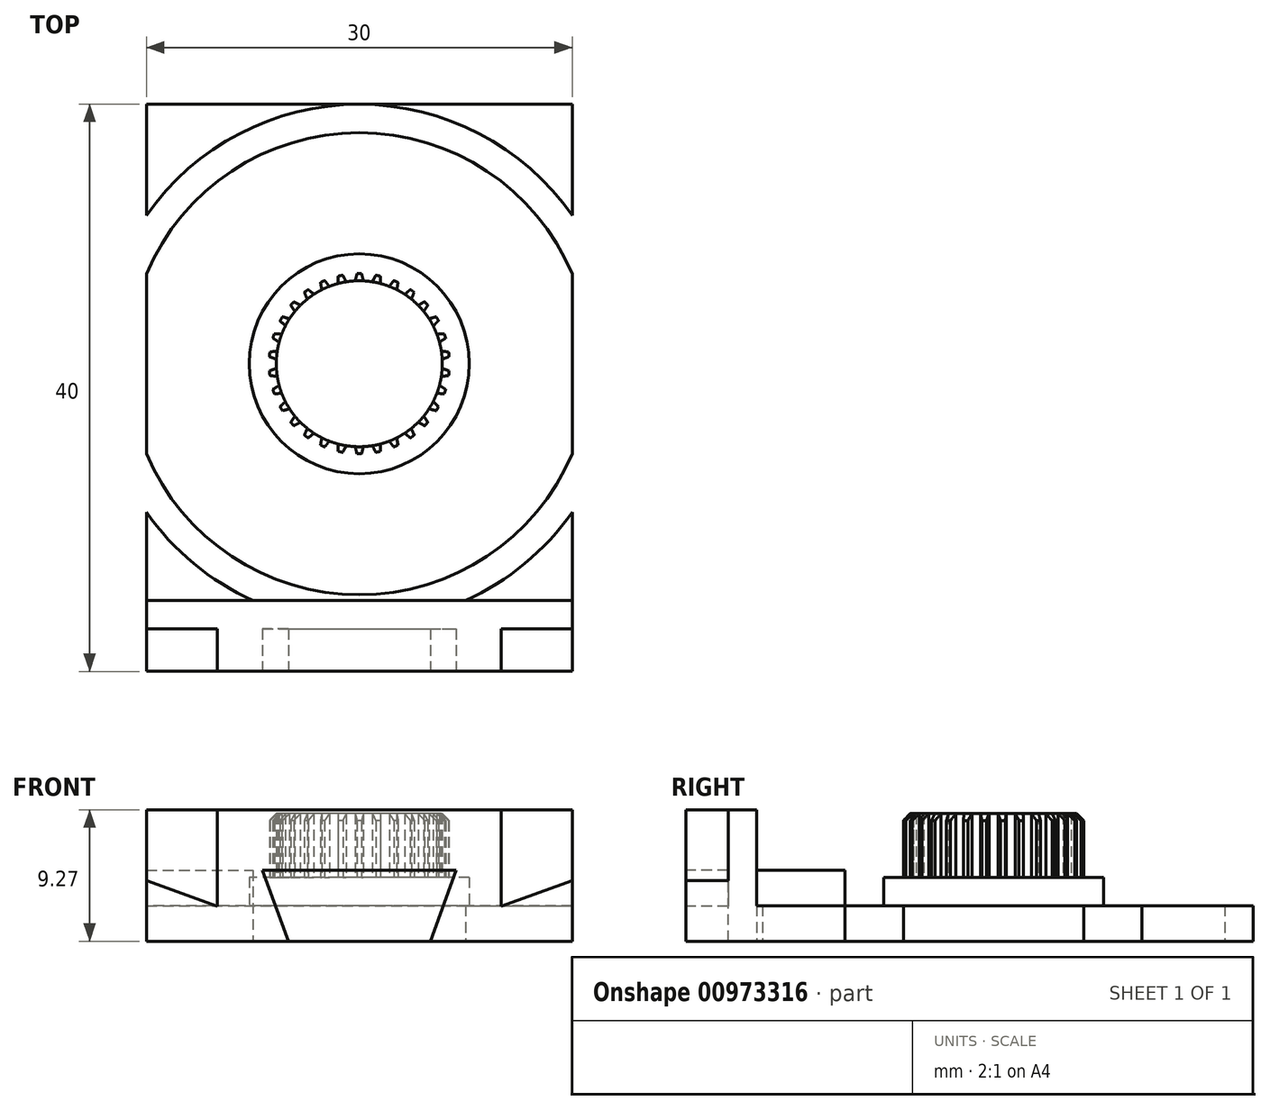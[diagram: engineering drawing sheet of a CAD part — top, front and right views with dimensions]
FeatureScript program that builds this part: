
annotation { "Feature Type Name" : "Feature", "Feature Type Description" : "" }
export const myFeature = defineFeature(function(context is Context, id is Id, definition is map)
    precondition{}
    {
        {
            var Q0;
            Q0=qCreatedBy(makeId("Top.planeOp"),FACE);
            var sketch = newSketch(context, id + "F0", { "sketchPlane" : qUnion([Q0])});
            skLineSegment(sketch, "E0.bottom", {"start": v(-15, 18.31) * mm, "end": v(15, 18.31) * mm});
            skLineSegment(sketch, "E0.top", {"start": v(-15, -21.69) * mm, "end": v(15, -21.69) * mm});
            skLineSegment(sketch, "E0.left", {"start": v(-15, 18.31) * mm, "end": v(-15, -21.69) * mm});
            skLineSegment(sketch, "E0.right", {"start": v(15, 18.31) * mm, "end": v(15, -21.69) * mm});
            skCircle(sketch, "E1", {"center": v(0, 0) * mm, "radius": 14.29 * mm, "construction": true});
            skLineSegment(sketch, "E2", {"start": v(-15, -16.69) * mm, "end": v(15, -16.69) * mm});
            skCircle(sketch, "E3", {"center": v(0, 0) * mm, "radius": 7.75 * mm});
            skCircle(sketch, "E4", {"center": v(0, 0) * mm, "radius": 6.35 * mm});
            skCircle(sketch, "E5", {"center": v(0, 0) * mm, "radius": 5.85 * mm});
            skLineSegment(sketch, "E6", {"start": v(6.33, 0.5) * mm, "end": v(5.84, 0.32) * mm});
            skLineSegment(sketch, "E7.MirrorCS", {"start": v(6.33, -0.5) * mm, "end": v(5.84, -0.32) * mm});
            skLineSegment(sketch, "E8", {"start": v(0, 0) * mm, "end": v(0, 18.29) * mm, "construction": true});
            skLineSegment(sketch, "E9", {"start": v(0, 0) * mm, "end": v(0, -14.29) * mm, "construction": true});
            skPoint(sketch, "E10.start.orphan", {"position": v(-15, 0) * mm});
            skCircle(sketch, "E11", {"center": v(0, 0) * mm, "radius": 16.29 * mm});
            skCircle(sketch, "E12", {"center": v(0, 0) * mm, "radius": 18.29 * mm});
            skSolve(sketch);
        }
        {
            var Q0;
            Q0=makeQuery(id+"F0.imprint","IMPRINT",FACE,{"disambiguationData":[TD([[makeQuery(id+"F0.imprint","IMPRINT",EDGE,{"derivedFrom":sQuery(id+"F0.wireOp",EDGE,"vQMhKaP6-cxV4-EDMz-RZqz-IjqFTc3130Nv")}),-1.0]])]});
            var Q1;
            Q1=makeQuery(id+"F0.imprint","IMPRINT",FACE,{"disambiguationData":[TD([[makeQuery(id+"F0.imprint","IMPRINT",EDGE,{"derivedFrom":sQuery(id+"F0.wireOp",EDGE,"E3")}),-1.0]])]});
            var Q2;
            {var subQ0=sQuery(id+"F0.wireOp",EDGE,"E2");Q2=makeQuery(id+"F0.imprint","IMPRINT",FACE,{"disambiguationData":[TD([[makeQuery(id+"F0.imprint","IMPRINT",EDGE,{"derivedFrom":subQ0}),1.0]])]});}
            var Q3;
            {var subQ1=sQuery(id+"F0.wireOp",EDGE,"E0.left");var subQ5=sQuery(id+"F0.wireOp",EDGE,"E12");var subQ10=makeQuery(id+"F0.imprint","INTERSECT",VERTEX,{"disambiguationData":[OD(1.0)],"derivedFrom":[subQ1,subQ5]});Q3=makeQuery(id+"F0.imprint","IMPRINT",FACE,{"disambiguationData":[TD([[makeQuery(id+"F0.imprint","IMPRINT",EDGE,{"disambiguationData":[TD([[subQ10,1.0]])],"derivedFrom":subQ1}),1.0]])]});}
            extrude(context, id + "F1", {"entities" : qUnion([Q0, Q1, Q2, Q3]), "depth" : 2.5 * mm, "offsetDistance" : 25 * mm});
        }
        {
            var Q0;
            Q0=makeQuery(id+"F0.imprint","IMPRINT",FACE,{"disambiguationData":[TD([[makeQuery(id+"F0.imprint","IMPRINT",EDGE,{"derivedFrom":sQuery(id+"F0.wireOp",EDGE,"E3")}),1.0]])]});
            extrude(context, id + "F2", {"entities" : qUnion([Q0]), "operationType" : NewBodyOperationType.ADD, "depth" : 4.5 * mm, "offsetDistance" : 25 * mm});
        }
        {
            var Q0;
            Q0=makeQuery(id+"F0.imprint","IMPRINT",FACE,{"disambiguationData":[TD([[makeQuery(id+"F0.imprint","IMPRINT",EDGE,{"derivedFrom":sQuery(id+"F0.wireOp",EDGE,"E4")}),1.0]])]});
            var Q1;
            {var subQ0=sQuery(id+"F0.wireOp",EDGE,"E5");var subQ1=makeQuery(id+"F0.imprint","INTERSECT",VERTEX,{"derivedFrom":[subQ0,sQuery(id+"F0.wireOp",EDGE,"E6")]});Q1=makeQuery(id+"F0.imprint","IMPRINT",FACE,{"disambiguationData":[TD([[makeQuery(id+"F0.imprint","IMPRINT",EDGE,{"disambiguationData":[TD([[subQ1,-1.0]])],"derivedFrom":subQ0}),1.0]])]});}
            extrude(context, id + "F3", {"entities" : qUnion([Q0, Q1]), "operationType" : NewBodyOperationType.ADD, "depth" : 9 * mm, "offsetDistance" : 25 * mm});
        }
        {
            var Q0;
            {var subQ0=sQuery(id+"F0.wireOp",EDGE,"E0.top");Q0=makeQuery(id+"F0.imprint","IMPRINT",FACE,{"disambiguationData":[TD([[makeQuery(id+"F0.imprint","IMPRINT",EDGE,{"derivedFrom":subQ0}),1.0]])]});}
            var Q1;
            {var subQ0=sQuery(id+"F0.wireOp",EDGE,"E12");var subQ1=sQuery(id+"F0.wireOp",EDGE,"E2");var subQ2=makeQuery(id+"F0.imprint","INTERSECT",VERTEX,{"disambiguationData":[OD(0.0)],"derivedFrom":[subQ1,subQ0]});Q1=makeQuery(id+"F0.imprint","IMPRINT",FACE,{"disambiguationData":[TD([[makeQuery(id+"F0.imprint","IMPRINT",EDGE,{"disambiguationData":[TD([[subQ2,-1.0]])],"derivedFrom":subQ1}),-1.0]])]});}
            extrude(context, id + "F4", {"entities" : qUnion([Q0, Q1]), "operationType" : NewBodyOperationType.ADD, "depth" : 9.27 * mm, "offsetDistance" : 25 * mm});
        }
        {
            var Q0;
            Q0=makeQuery(id+"F3.opExtrude","CAP_EDGE",EDGE,{"disambiguationData":[OSD([sQuery(id+"F0.wireOp",EDGE,"E4")])],"isStart":false});
            chamfer(context, id + "F5", {"entities" : qUnion([Q0]), "width" : .5 * mm, "tangentPropagation" : true});
        }
        {
            var Q0;
            {var subQ0=sQuery(id+"F0.wireOp",EDGE,"E6");Q0=makeQuery(id+"F0.imprint","IMPRINT",FACE,{"disambiguationData":[TD([[makeQuery(id+"F0.imprint","IMPRINT",EDGE,{"derivedFrom":subQ0}),1.0]])]});}
            extrude(context, id + "F6", {"entities" : qUnion([Q0]), "operationType" : NewBodyOperationType.REMOVE, "depth" : 9 * mm, "offsetDistance" : 25 * mm, "hasSecondDirection" : true, "secondDirectionOppositeDirection" : false, "secondDirectionDepth" : 4.5 * mm});
        }
        {
            var Q0;
            Q0=makeQuery(id+"F6.boolean.opBoolean","COPY",FACE,{"derivedFrom":makeQuery(id+"F6.opExtrude","SWEPT_FACE",FACE,{"disambiguationData":[OSD([sQuery(id+"F0.wireOp",EDGE,"E5")])]})});
            var Q1;
            Q1=makeQuery(id+"F6.boolean.opBoolean","COPY",FACE,{"derivedFrom":makeQuery(id+"F6.opExtrude","SWEPT_FACE",FACE,{"disambiguationData":[OSD([sQuery(id+"F0.wireOp",EDGE,"E6")])]})});
            var Q2;
            Q2=makeQuery(id+"F6.boolean.opBoolean","COPY",FACE,{"derivedFrom":makeQuery(id+"F6.opExtrude","SWEPT_FACE",FACE,{"disambiguationData":[OSD([sQuery(id+"F0.wireOp",EDGE,"E7.MirrorCS")])]})});
            var Q3;
            Q3=makeQuery(id+"F3.opExtrude","SWEPT_FACE",FACE,{"disambiguationData":[OSD([sQuery(id+"F0.wireOp",EDGE,"E4")])]});
            circularPattern(context, id + "F7", {"patternType" : PatternType.FACE, "faces" : qUnion([Q0, Q1, Q2]), "axis" : qUnion([Q3]), "angle" : 360 * degree, "instanceCount" : 30, "equalSpace" : true});
        }
        {
            var Q0;
            Q0=makeQuery(id+"F4.opExtrude","SWEPT_FACE",FACE,{"disambiguationData":[OSD([sQuery(id+"F0.wireOp",EDGE,"E0.top")])]});
            var sketch = newSketch(context, id + "F8", { "sketchPlane" : qUnion([Q0])});
            skLineSegment(sketch, "E13", {"start": v(0, 9.27) * mm, "end": v(0, 0) * mm, "construction": true});
            skLineSegment(sketch, "E14.bottom", {"start": v(-5, 0) * mm, "end": v(5, 0) * mm});
            skLineSegment(sketch, "E14.top", {"start": v(-5, 5) * mm, "end": v(5, 5) * mm});
            skLineSegment(sketch, "E14.left", {"start": v(-5, 0) * mm, "end": v(-5, 5) * mm});
            skLineSegment(sketch, "E14.right", {"start": v(5, 0) * mm, "end": v(5, 5) * mm});
            skLineSegment(sketch, "E15", {"start": v(-5, 0) * mm, "end": v(-6.82, 5) * mm});
            skLineSegment(sketch, "E16", {"start": v(-5, 5) * mm, "end": v(-6.82, 5) * mm});
            skLineSegment(sketch, "E17.MirrorCS", {"start": v(5, 0) * mm, "end": v(6.82, 5) * mm});
            skLineSegment(sketch, "E18.MirrorCS", {"start": v(5, 5) * mm, "end": v(6.82, 5) * mm});
            skLineSegment(sketch, "E19.bottom", {"start": v(-15, 9.27) * mm, "end": v(-10, 9.27) * mm});
            skLineSegment(sketch, "E19.top", {"start": v(-15, 4.27) * mm, "end": v(-10, 4.27) * mm});
            skLineSegment(sketch, "E19.left", {"start": v(-15, 9.27) * mm, "end": v(-15, 4.27) * mm});
            skLineSegment(sketch, "E19.right", {"start": v(-10, 9.27) * mm, "end": v(-10, 4.27) * mm});
            skLineSegment(sketch, "E20", {"start": v(-10, 4.27) * mm, "end": v(-10, 2.45) * mm});
            skLineSegment(sketch, "E21", {"start": v(-15, 4.27) * mm, "end": v(-10, 2.45) * mm});
            skLineSegment(sketch, "E22.MirrorCS", {"start": v(10, 9.27) * mm, "end": v(10, 4.27) * mm});
            skLineSegment(sketch, "E23.MirrorCS", {"start": v(10, 4.27) * mm, "end": v(10, 2.45) * mm});
            skLineSegment(sketch, "E24.MirrorCS", {"start": v(15, 4.27) * mm, "end": v(10, 2.45) * mm});
            skLineSegment(sketch, "E25.MirrorCS", {"start": v(15, 9.27) * mm, "end": v(10, 9.27) * mm});
            skLineSegment(sketch, "E26.MirrorCS", {"start": v(15, 9.27) * mm, "end": v(15, 4.27) * mm});
            skSolve(sketch);
        }
        {
            var Q0;
            Q0=makeQuery(id+"F8.imprint","IMPRINT",FACE,{"disambiguationData":[TD([[makeQuery(id+"F8.imprint","IMPRINT",EDGE,{"derivedFrom":sQuery(id+"F8.wireOp",EDGE,"E14.right")}),-1.0]])]});
            var Q1;
            Q1=makeQuery(id+"F8.imprint","IMPRINT",FACE,{"disambiguationData":[TD([[makeQuery(id+"F8.imprint","IMPRINT",EDGE,{"derivedFrom":sQuery(id+"F8.wireOp",EDGE,"E14.bottom")}),1.0]])]});
            var Q2;
            Q2=makeQuery(id+"F8.imprint","IMPRINT",FACE,{"disambiguationData":[TD([[makeQuery(id+"F8.imprint","IMPRINT",EDGE,{"derivedFrom":sQuery(id+"F8.wireOp",EDGE,"E14.left")}),1.0]])]});
            var Q3;
            Q3=makeQuery(id+"F8.imprint","IMPRINT",FACE,{"disambiguationData":[TD([[makeQuery(id+"F8.imprint","IMPRINT",EDGE,{"derivedFrom":sQuery(id+"F8.wireOp",EDGE,"E19.bottom")}),-1.0]])]});
            var Q4;
            Q4=makeQuery(id+"F8.imprint","IMPRINT",FACE,{"disambiguationData":[TD([[makeQuery(id+"F8.imprint","IMPRINT",EDGE,{"derivedFrom":sQuery(id+"F8.wireOp",EDGE,"E19.top")}),-1.0]])]});
            var Q5;
            Q5=makeQuery(id+"F8.imprint","IMPRINT",FACE,{"disambiguationData":[TD([[makeQuery(id+"F8.imprint","IMPRINT",EDGE,{"derivedFrom":sQuery(id+"F8.wireOp",EDGE,"E22.MirrorCS")}),1.0]])]});
            extrude(context, id + "F9", {"entities" : qUnion([Q0, Q1, Q2, Q3, Q4, Q5]), "operationType" : NewBodyOperationType.REMOVE, "oppositeDirection" : true, "depth" : 3 * mm, "offsetDistance" : 25 * mm});
        }
        {
            var Q0;
            {var subQ0=sQuery(id+"F0.wireOp",EDGE,"E12");var subQ1=sQuery(id+"F0.wireOp",EDGE,"E0.left");var subQ2=makeQuery(id+"F0.imprint","INTERSECT",VERTEX,{"disambiguationData":[OD(0.0)],"derivedFrom":[subQ1,subQ0]});Q0=makeQuery(id+"F0.imprint","IMPRINT",FACE,{"disambiguationData":[TD([[makeQuery(id+"F0.imprint","IMPRINT",EDGE,{"disambiguationData":[TD([[subQ2,-1.0]])],"derivedFrom":subQ1}),1.0]])]});}
            extrude(context, id + "F10", {"entities" : qUnion([Q0]), "operationType" : NewBodyOperationType.ADD, "depth" : 5 * mm, "offsetDistance" : 25 * mm});
        }
    });
